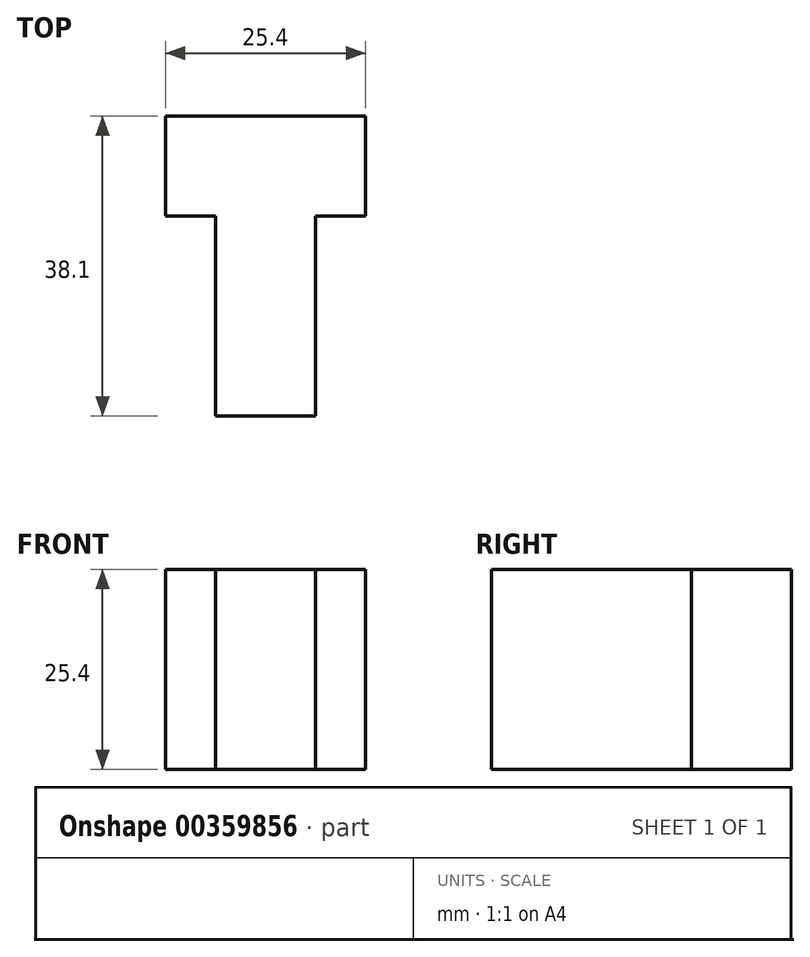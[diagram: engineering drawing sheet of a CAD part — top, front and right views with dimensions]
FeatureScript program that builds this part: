
annotation { "Feature Type Name" : "Feature", "Feature Type Description" : "" }
export const myFeature = defineFeature(function(context is Context, id is Id, definition is map)
    precondition{}
    {
        {
            var Q0;
            Q0=qCreatedBy(makeId("Top.planeOp"),FACE);
            var sketch = newSketch(context, id + "F0", { "sketchPlane" : qUnion([Q0])});
            skLineSegment(sketch, "E0", {"start": v(24.31, 0) * mm, "end": v(24.31, 25.4) * mm});
            skLineSegment(sketch, "E1", {"start": v(24.31, 25.4) * mm, "end": v(30.66, 25.4) * mm});
            skLineSegment(sketch, "E2", {"start": v(30.66, 25.4) * mm, "end": v(30.66, 38.1) * mm});
            skLineSegment(sketch, "E3", {"start": v(30.66, 38.1) * mm, "end": v(5.26, 38.1) * mm});
            skLineSegment(sketch, "E4", {"start": v(5.26, 38.1) * mm, "end": v(5.26, 25.4) * mm});
            skLineSegment(sketch, "E5", {"start": v(5.26, 25.4) * mm, "end": v(11.61, 25.4) * mm});
            skLineSegment(sketch, "E6", {"start": v(11.61, 25.4) * mm, "end": v(11.61, 0) * mm});
            skLineSegment(sketch, "E7", {"start": v(11.61, 0) * mm, "end": v(24.31, 0) * mm});
            skSolve(sketch);
        }
        {
            var Q0;
            Q0 = qSketchRegion(id + "F0", true);
            extrude(context, id + "F1", {"entities" : qUnion([Q0]), "depth" : 25.4 * mm});
        }
    });
